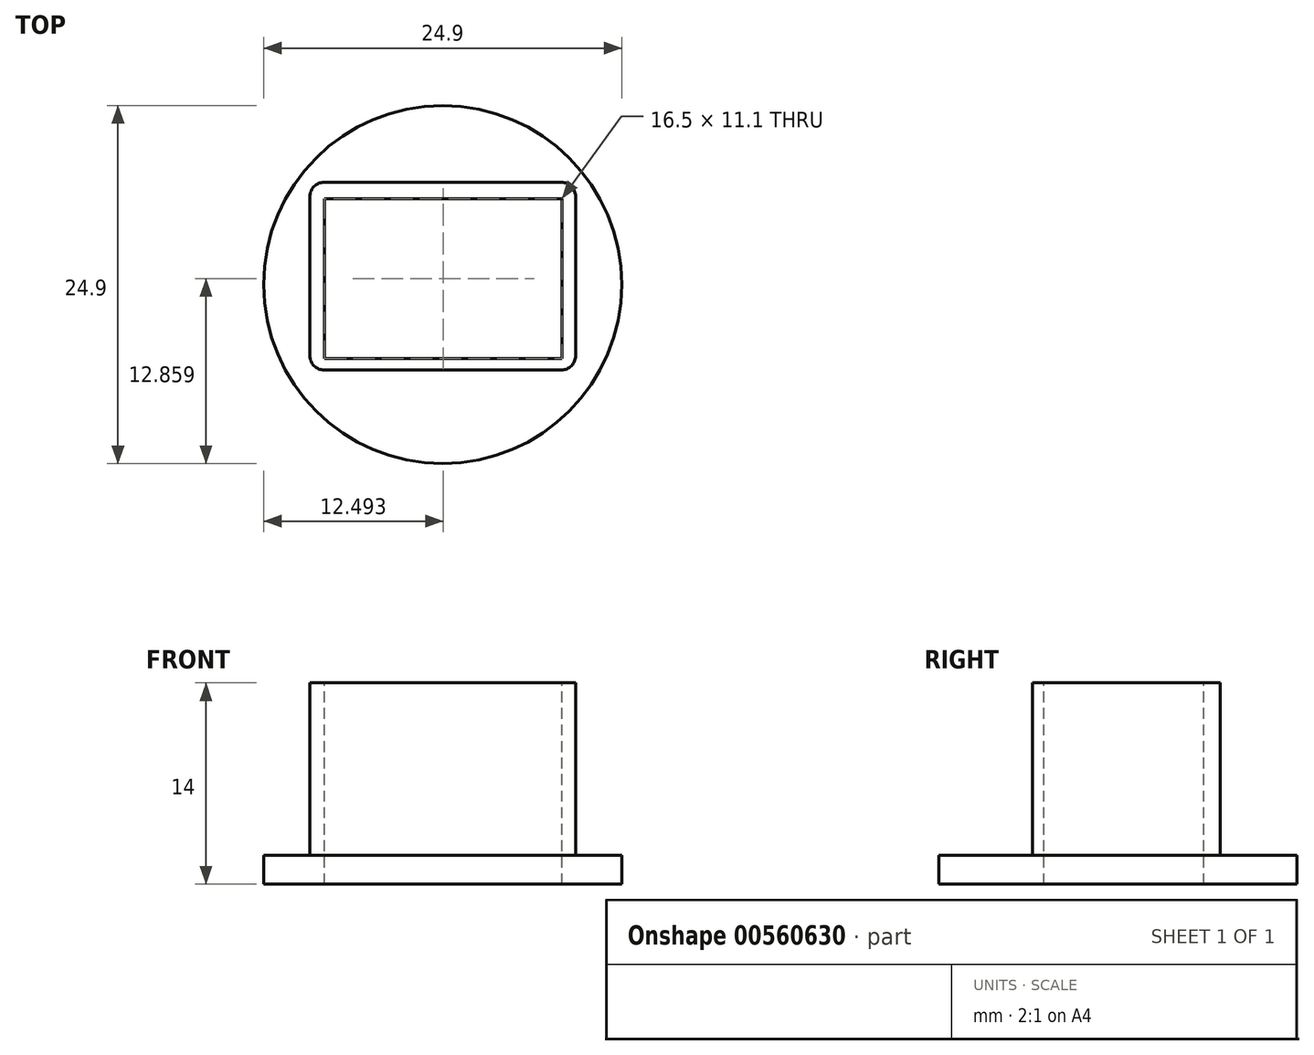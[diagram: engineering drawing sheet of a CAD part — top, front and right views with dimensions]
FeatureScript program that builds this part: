
annotation { "Feature Type Name" : "Feature", "Feature Type Description" : "" }
export const myFeature = defineFeature(function(context is Context, id is Id, definition is map)
    precondition{}
    {
        {
            var Q0;
            Q0=qCreatedBy(makeId("Top.planeOp"),FACE);
            var sketch = newSketch(context, id + "F0", { "sketchPlane" : qUnion([Q0])});
            skCircle(sketch, "E0", {"center": v(0, 0) * mm, "radius": 12.45 * mm});
            skSolve(sketch);
        }
        {
            var Q0;
            Q0 = qSketchRegion(id + "F0", true);
            extrude(context, id + "F1", {"entities" : qUnion([Q0]), "depth" : 2 * mm, "offsetDistance" : 25 * mm});
        }
        {
            var Q0;
            Q0=makeQuery(id+"F1.opExtrude","CAP_FACE",FACE,{"disambiguationData":[OSD([sQuery(id+"F0.wireOp",EDGE,"E0")])],"isStart":false});
            var sketch = newSketch(context, id + "F2", { "sketchPlane" : qUnion([Q0])});
            skLineSegment(sketch, "E1.bottom", {"start": v(-8.2, 5.96) * mm, "end": v(8.3, 5.96) * mm});
            skLineSegment(sketch, "E1.top", {"start": v(-8.2, -5.14) * mm, "end": v(8.3, -5.14) * mm});
            skLineSegment(sketch, "E1.left", {"start": v(-8.2, 5.96) * mm, "end": v(-8.2, -5.14) * mm});
            skLineSegment(sketch, "E1.right", {"start": v(8.3, 5.96) * mm, "end": v(8.3, -5.14) * mm});
            skSolve(sketch);
        }
        {
            var Q0;
            Q0 = qSketchRegion(id + "F2", true);
            extrude(context, id + "F3", {"entities" : qUnion([Q0]), "operationType" : NewBodyOperationType.REMOVE, "oppositeDirection" : true, "depth" : 2 * mm, "offsetDistance" : 25 * mm});
        }
        {
            var Q0;
            Q0=makeQuery(id+"F1.opExtrude","CAP_FACE",FACE,{"disambiguationData":[OSD([sQuery(id+"F0.wireOp",EDGE,"E0")])],"isStart":false});
            var sketch = newSketch(context, id + "F4", { "sketchPlane" : qUnion([Q0])});
            skLineSegment(sketch, "E2.bottom", {"start": v(-8.23, 7.1) * mm, "end": v(8.24, 7.1) * mm});
            skLineSegment(sketch, "E2.top", {"start": v(-8.23, -5.94) * mm, "end": v(8.24, -5.94) * mm});
            skLineSegment(sketch, "E2.left", {"start": v(-9.23, 6.1) * mm, "end": v(-9.23, -4.94) * mm});
            skLineSegment(sketch, "E2.right", {"start": v(9.24, 6.1) * mm, "end": v(9.24, -4.94) * mm});
            skPoint(sketch, "E3.visualSharp", {"position": v(-9.23, 7.1) * mm});
            skArc(sketch, "E3.filletArc", {"start": v(-8.23, 7.1) * mm, "mid": v(-8.94, 6.82) * mm, "end": v(-9.23, 6.1) * mm});
            skPoint(sketch, "E4.visualSharp", {"position": v(9.24, 7.1) * mm});
            skArc(sketch, "E4.filletArc", {"start": v(9.24, 6.1) * mm, "mid": v(8.95, 6.82) * mm, "end": v(8.24, 7.1) * mm});
            skPoint(sketch, "E5.visualSharp", {"position": v(9.24, -5.94) * mm});
            skArc(sketch, "E5.filletArc", {"start": v(8.24, -5.94) * mm, "mid": v(8.95, -5.65) * mm, "end": v(9.24, -4.94) * mm});
            skPoint(sketch, "E6.visualSharp", {"position": v(-9.23, -5.94) * mm});
            skArc(sketch, "E6.filletArc", {"start": v(-9.23, -4.94) * mm, "mid": v(-8.94, -5.65) * mm, "end": v(-8.23, -5.94) * mm});
            skSolve(sketch);
        }
        {
            var Q0;
            Q0=makeQuery(id+"F4.imprint","IMPRINT",FACE,{"disambiguationData":[TD([[makeQuery(id+"F4.imprint","IMPRINT",EDGE,{"derivedFrom":sQuery(id+"F4.wireOp",EDGE,"E2.bottom")}),-1.0]])]});
            extrude(context, id + "F5", {"entities" : qUnion([Q0]), "operationType" : NewBodyOperationType.ADD, "depth" : 12 * mm, "offsetDistance" : 25 * mm});
        }
    });
